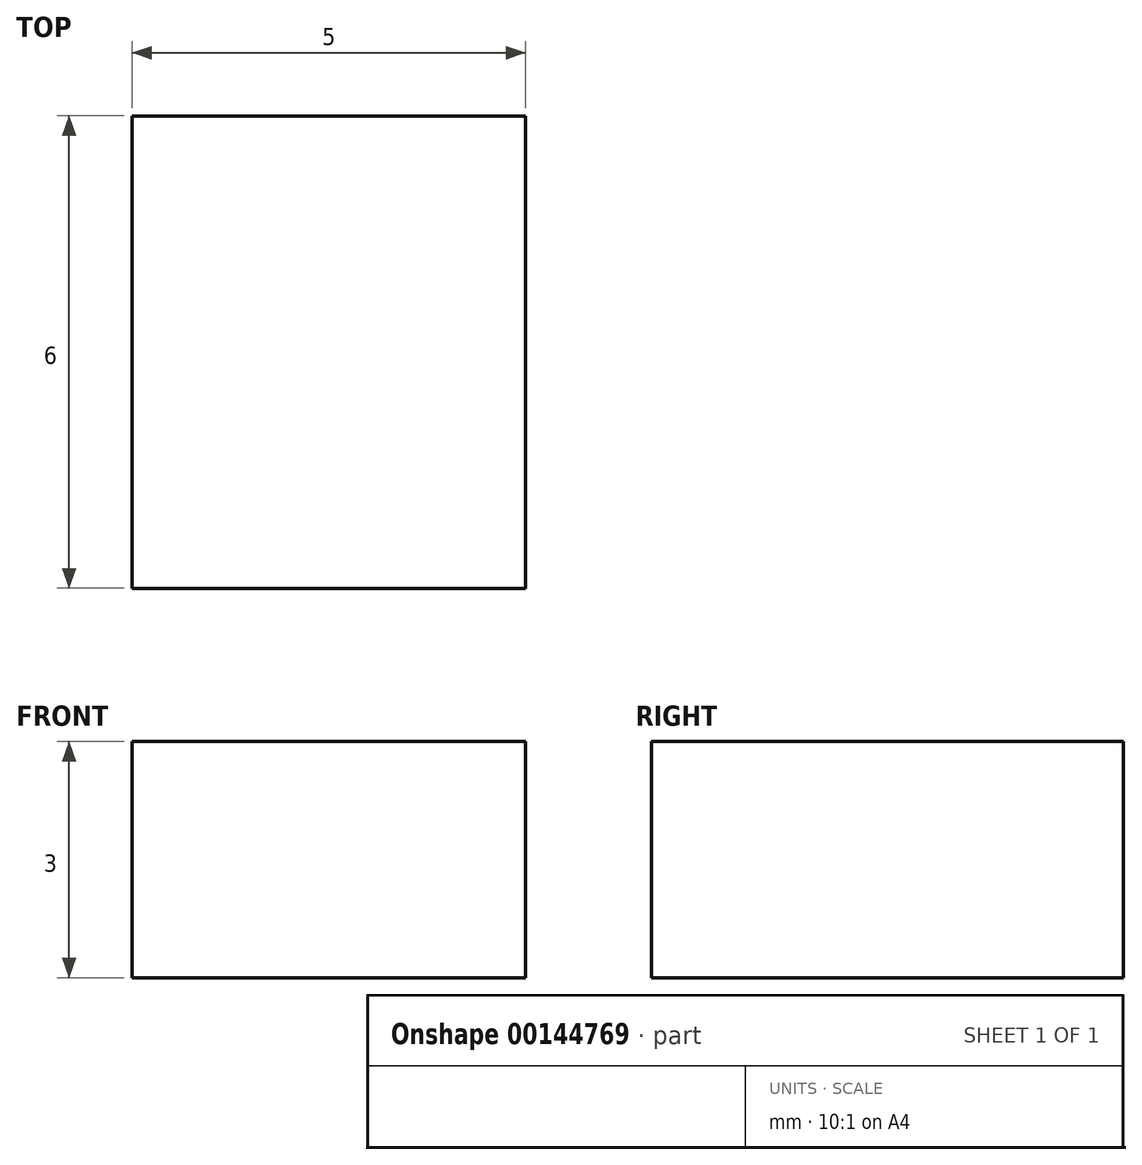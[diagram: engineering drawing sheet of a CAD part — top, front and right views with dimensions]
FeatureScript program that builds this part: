
annotation { "Feature Type Name" : "Feature", "Feature Type Description" : "" }
export const myFeature = defineFeature(function(context is Context, id is Id, definition is map)
    precondition{}
    {
        {
            var Q0;
            Q0=qCreatedBy(makeId("Top.planeOp"),FACE);
            var sketch = newSketch(context, id + "F0", { "sketchPlane" : qUnion([Q0])});
            skLineSegment(sketch, "E0.bottom", {"start": v(-12.71, 6.17) * mm, "end": v(14, 6.17) * mm});
            skLineSegment(sketch, "E0.top", {"start": v(-12.71, 31.22) * mm, "end": v(14, 31.22) * mm});
            skLineSegment(sketch, "E0.left", {"start": v(-12.71, 6.17) * mm, "end": v(-12.71, 31.22) * mm});
            skLineSegment(sketch, "E0.right", {"start": v(14, 6.17) * mm, "end": v(14, 31.22) * mm});
            skLineSegment(sketch, "E1.bottom", {"start": v(-42.92, 35.28) * mm, "end": v(-37.92, 35.28) * mm});
            skLineSegment(sketch, "E1.top", {"start": v(-42.92, 41.28) * mm, "end": v(-37.92, 41.28) * mm});
            skLineSegment(sketch, "E1.left", {"start": v(-42.92, 35.28) * mm, "end": v(-42.92, 41.28) * mm});
            skLineSegment(sketch, "E1.right", {"start": v(-37.92, 35.28) * mm, "end": v(-37.92, 41.28) * mm});
            skSolve(sketch);
        }
        {
            var Q0;
            Q0=makeQuery(id+"F0.imprint","IMPRINT",FACE,{"disambiguationData":[TD([[makeQuery(id+"F0.imprint","IMPRINT",EDGE,{"derivedFrom":sQuery(id+"F0.wireOp",EDGE,"E1.bottom")}),1.0]])]});
            extrude(context, id + "F1", {"entities" : qUnion([Q0]), "depth" : 3 * mm});
        }
    });
